# Revit family: IS_CerathermT25_A7544_BIM_NL
name_source: partatom
category: Plumbing Fixtures
units: mm (PartAtom-declared; Revit-internal decimal feet)

## family parameters
Always vertical = No
Cut with Voids When Loaded = No
OmniClass Number = 23.45.55.17
OmniClass Title = Mixing Faucets
Part Type = Normal
Room Calculation Point = No
Round Connector Dimension = Use Diameter
Shared = No
Work Plane-Based = No

## types (1)
- A7544XG - CERATHERM RIM-MOUNTED T25 THERMOSTATIC BATH & SHOWER EXP - SILK BLACK
    Accesoires = https://www.idealstandard.nl
    Accessories = https://www.idealstandard.nl
    Afmetingen = 314 x 185 x 70 mm
    AfstandsEenheid = Millimeter
    Afwerking = Seide schwarz
    AreaUnits = Millimetres
    Artikelnummer = A7544XG
    Artikelomschrijving = CERATHERM RIM-MONTIERTE T25 THERMOSTATISCHE BAD & DUSCHE EXP
    Artikelreferentie = CERATHERM RIM-MOUNTED T25 THERMOSTATIC BATH & SHOWER EXP
    Auteur = Ideal Standard
    BIMObjectName = IS_IdealStandard_Showermixers_CerathermT25_A7544
    BIMobject category = Sanitary
    BIMobject category code = Taps & Mixers
    BIMobject main category = Sanitary
    BarCode = 4015413350556
    Barcode = 4015413350556
    Bedieningkraan = Handbuch
    Bedieningkraanwerk = drehen wissen
    Beschrijvingdouchekop = Regenbrause
    Beschrijvinggarantie = Herstellergarantie
    BimObjectNaam = IS_IdealStandard_Showermixers_CerathermT25_A7544
    Brand = Ideal Standard
    Brand url = http://www.idealstandard.nl
    Breedte = 314.409857
    BrutoGewicht = 0
    Color = Seide schwarz
    ConnectionType = Installation
    Cost = 0 $
    CurrencyUnit = €
    CurrentRevision = 1
    Date of publishing = 24/07/2021
    Description = CERATHEM RIM-MONTIERTE T25 THERMOSTATISCHE BAD & DUSCHE EXP - SEIDE SCHWARZ
    Diepte = 185 mm
    Douchebak = No
    DurationUnit = Years
    Edition number = 1
    Eigenschappen = RIM-MONTIERTE T25 THERMOSTATISCHE BAD & DUSCHE EXP - SEIDE SCHWARZ
    FaucetFunction = Mixer
    FaucetOperation = Turning Knobs Controless
    FaucetType = Thermostatic Mixer
    Features = RIM-MONTIERTE T25 THERMOSTATISCHE BAD & DUSCHE EXP - SEIDE SCHWARZ
    Finish = Seide schwarz
    Functieindoucheruimte = Thermostat-Brausemischer
    Functiekraanwerk = Thermostat-Brausemischer
    GTIN code = https://4015413350556
    Garantieonderdelen = 5
    Garantieunits = Jaren
    GemaaktOp = 27/07/2021
    HasIntegralShutOffDevice = No
    Help = https://www.idealstandard.nl
    Hoogte = 70.09403
    Hulp = https://www.idealstandard.nl
    IFC Classification = Sanitary Terminal
    IfcExportAs = IfcValveType
    IfcExportType = MIXING
    Installatieinstructies = https://www.idealstandard.nl
    Installation instructions = https://www.idealstandard.nl
    InstallationInstructions = https://www.idealstandard.nl
    IsBuiltIn = No
    IsHighPressure = No
    Klepmechanisme = Drehknöpfe Controlless
    Kleur = Seide schwarz
    Lengte = 0 mm  [stored 0 ft]
    LinearUnits = Millimetres
    MainColor = Seide schwarz
    MaintenanceInformation = https://www.idealstandard.nl
    Manufacturer = Ideal Standard
    Manufacturer name = Ideal Standard
    ManufacturerURL = https://www.idealstandard.nl
    Materiaal = Messing
    Material = Brass
    Material main = Brass
    Merk = Ideal Standard
    Model = A7544XG
    ModelNumber = A7544XG
    ModelReference = CERATHERM RIM-MOUNTED T25 THERMOSTATIC BATH & SHOWER EXP
    Montageinstuctie = https://www.idealstandard.nl
    NBS Reference Code = 45-35-70/335
    NBS Reference Description = Shower mixers
    Name = Showermixers_CerathermT25_A7544_IdealStandard
    NettWeight = 1.95
    Nettogewicht = 1.95
    NominalDepth = 185 mm
    NominalHeight = 70 mm
    NominalLength = 185 mm
    NominalWidth = 314 mm
    Normen = Showermixers_CerathermT25_A7544_IdealStandard
    OppervlakteEenheid = Millimeter
    Product Guid = 07dc37f9-d312-483b-acfa-6ee7a77236cb
    Product SKU = A7544
    Product certification = https://www.idealstandard.nl
    Product data url = https://bimobject.com
    Product family = Sanitary
    Product group = Showers
    Product name = CERATHERM RIM-MOUNTED T25 THERMOSTATIC BATH & SHOWER EXP
    Product url = https://www.idealstandard.nl
    ProductInformation = https://www.idealstandard.nl
    ProductSoort = Sanitary
    Productinformatie = https://www.idealstandard.nl
    QR code = http://bimobject.com
    Referentie = CERATHEM RIM-MOUNTED T25 THERMOSTATIC BATH & SHOWER EXP
    Revisie = 1
    Shape = Cylindrical
    ShowerType = Thermostatic Shower Mixer
    Size = 314 x 185 x 70 mm
    Space = Internal
    SpareParts = https://www.idealstandard.nl
    Technical description = https://www.idealstandard.nl
    Telefoonnummer = 077 355 08 08
    TestPressure = 10 Bar
    Testdruk = 10 Bar
    Typeconnectie = Installation
    URL = https://www.idealstandard.nl
    Uniclass 2.0 Code = PR-35-06-82
    Uniclass 2.0 Description = Shower Mixer
    Uniclass 2015 Code = Pr_40_20_87_80
    Uniclass 2015 Name = Shower thermostatic valves
    Uniclass2015Beschrijving = Shower thermostatic valves
    Uniclass2015Code = Pr_40_20_87_80
    Uniclass2015Referentie = Pr_40_20_87_80
    Uniclass2015Title = Shower thermostatic valves
    Uniclass2015Version = v1.22
    Urlproducent = https://www.idealstandard.nl
    ValutaEenheid = Euro
    Versie = 1
    Version = 1
    Vervangingskosten = 0
    VolumeUnits = Litres
    Volumeunits = Liters
    Vorm = zylindrisch
    WRASURL = https://www.wrasapprovals.co.uk
    WarrantyDescription = Manufacturer warranty
    WarrantyDurationUnit = Years
    Wisselstukken = https://www.idealstandard.nl
    Youtube clip = https://www.youtube.com

note: [stored X ft] marks values corroborated as IEEE doubles in the binary element streams (Revit-internal decimal feet)

## geometry (parser evidence)
native form markers: Sweep x3
no freeform markers — native parametric forms only
